# Revit family: Shower-Valve_Trim-KOHLER-PURIST-C14488W_1
name_source: partatom
category: Plumbing Fixtures
revit_build: Autodesk Revit 2017 (Build: 20160225_1515(x64)
units: mm (PartAtom-declared; Revit-internal decimal feet)

## family parameters
Cut with Voids When Loaded = No
Host = Face
OmniClass Number = 23.31.17.00
OmniClass Title = Showers
Part Type = Normal
Room Calculation Point = No
Round Connector Dimension = Use Diameter
Shared = No

## types (2) — shared parameters
ADA Compliant = No
Assembly Code = D2010700
CW Connection = Yes
Cold Water Inlet = Cold Water Inlet
Date Modified = 07/20/2021
Default Elevation = 42"
Drain Included = No
Finish = Kohler-Metal-CP-Polished_Chrome
Flow Rate = 0 GPM
HW Connection = Yes
Height = 6 3/8"
Hot Water Inlet = Hot Water Inlet
Manufacturer = KOHLER Co.
Master Format 2014 = 22 42 23
Master Format 2014 Name = Residential Showers
Material = Premium Metal construction
Pressure = 0.00 psi
Product Name = PURIST
Tempered water Outlet = Tempered water Outlet
URL = https://www.kohler.co.uk
Vent Connection = No
Waste Connection = No
Waste Water Outlet = Waste Water Outlet
WaterSense Certified = No
Width = 6 3/8"

## per-type parameters (varying)
| type | Cross Handle | Description | Handle Clerance | Length | Lever Handle | Model | Type |
| Cross Handle, CP- Polished Chrome | Yes | CROSS THERMOSTATIC NO SHUT OFF | 1 3/4" | 3 15/16" | No | C14488W-3-CP | 1 |
| Lever Handle, CP- Polished Chrome | No | LEVER THERMOSTATIC NO SHUT OFF | 2 5/8" | 4 1/4" | Yes | C14488W-4-CP | 2 |

## geometry (parser evidence)
native form markers: Sweep x4
no freeform markers — native parametric forms only
